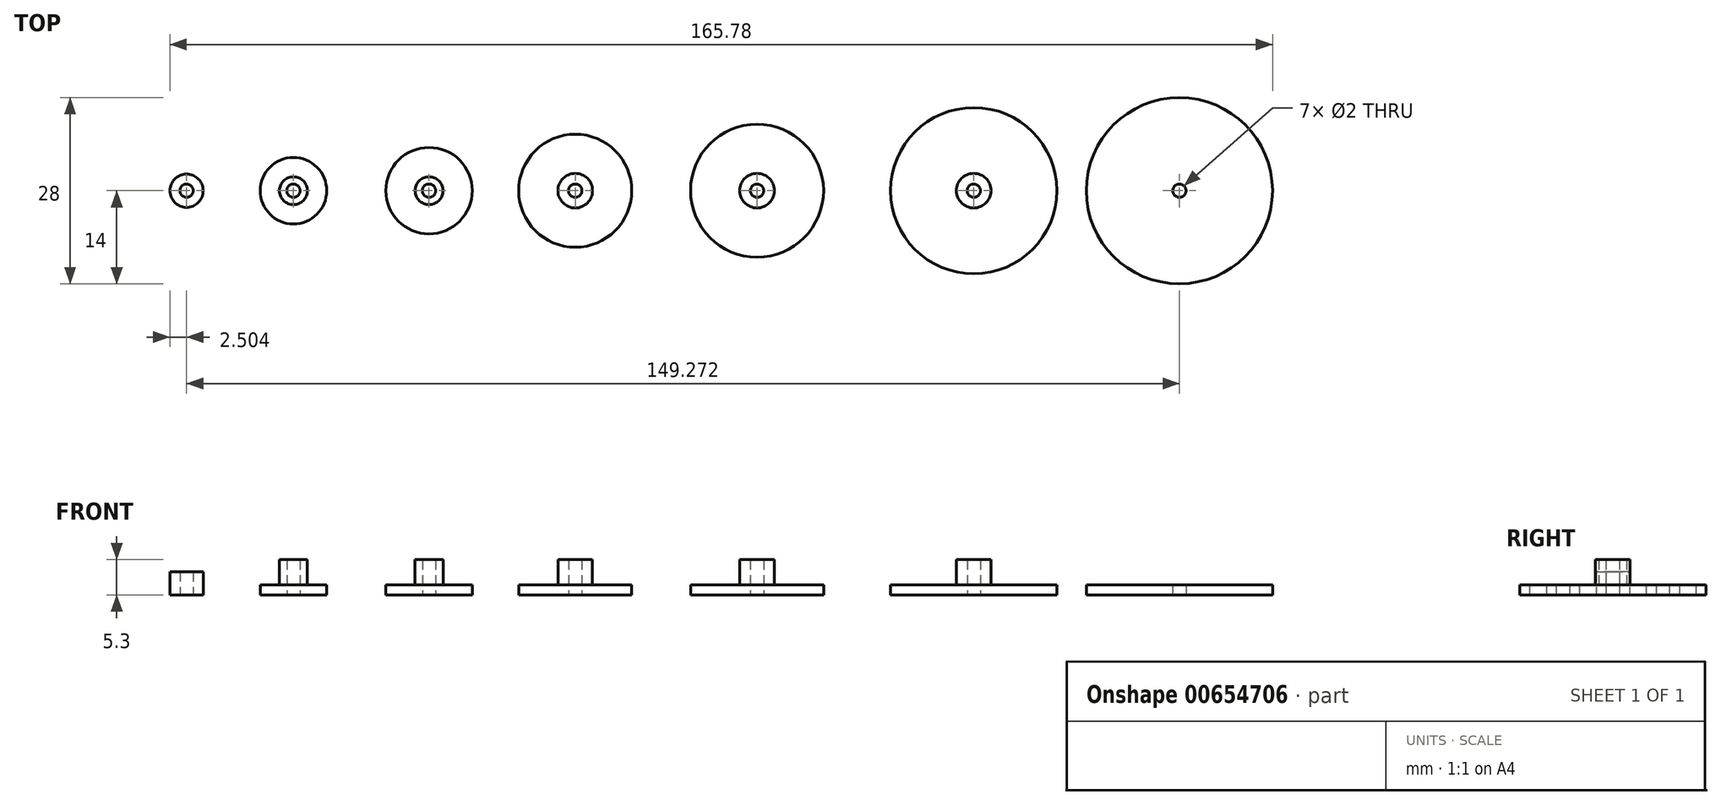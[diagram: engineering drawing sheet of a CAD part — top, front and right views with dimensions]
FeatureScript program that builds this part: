
annotation { "Feature Type Name" : "Feature", "Feature Type Description" : "" }
export const myFeature = defineFeature(function(context is Context, id is Id, definition is map)
    precondition{}
    {
        {
            var Q0;
            Q0=qCreatedBy(makeId("Top.planeOp"),FACE);
            var sketch = newSketch(context, id + "F0", { "sketchPlane" : qUnion([Q0])});
            skCircle(sketch, "E0", {"center": v(0, 0) * mm, "radius": 8.5 * mm});
            skCircle(sketch, "E1", {"center": v(0, 0) * mm, "radius": 1 * mm});
            skSolve(sketch);
        }
        {
            var Q0;
            Q0=makeQuery(id+"F0.imprint","IMPRINT",FACE,{"disambiguationData":[TD([[makeQuery(id+"F0.imprint","IMPRINT",EDGE,{"derivedFrom":sQuery(id+"F0.wireOp",EDGE,"E1")}),-1.0]])]});
            var Q1;
            {var subQ0=sQuery(id+"F0.wireOp",EDGE,"EI4zZE9N-whVI-OPHs-3LS9-Eucb53RtoGpZ");var subQ1=sQuery(id+"F0.wireOp",EDGE,"E0");var subQ2=makeQuery(id+"F0.imprint","INTERSECT",VERTEX,{"derivedFrom":[subQ1,subQ0]});Q1=makeQuery(id+"F0.imprint","IMPRINT",FACE,{"disambiguationData":[TD([[makeQuery(id+"F0.imprint","IMPRINT",EDGE,{"disambiguationData":[TD([[subQ2,1.0]])],"derivedFrom":subQ1}),-1.0]])]});}
            var Q2;
            {var subQ0=sQuery(id+"F0.wireOp",EDGE,"6d7b41f3-6400-49b5-a72e-f197a9a28993.24.0");var subQ1=sQuery(id+"F0.wireOp",EDGE,"E0");var subQ2=makeQuery(id+"F0.imprint","INTERSECT",VERTEX,{"derivedFrom":[subQ1,subQ0]});Q2=makeQuery(id+"F0.imprint","IMPRINT",FACE,{"disambiguationData":[TD([[makeQuery(id+"F0.imprint","IMPRINT",EDGE,{"disambiguationData":[TD([[subQ2,1.0]])],"derivedFrom":subQ1}),-1.0]])]});}
            var Q3;
            {var subQ0=sQuery(id+"F0.wireOp",EDGE,"6d7b41f3-6400-49b5-a72e-f197a9a28993.25.0");var subQ1=sQuery(id+"F0.wireOp",EDGE,"E0");var subQ2=makeQuery(id+"F0.imprint","INTERSECT",VERTEX,{"derivedFrom":[subQ1,subQ0]});Q3=makeQuery(id+"F0.imprint","IMPRINT",FACE,{"disambiguationData":[TD([[makeQuery(id+"F0.imprint","IMPRINT",EDGE,{"disambiguationData":[TD([[subQ2,1.0]])],"derivedFrom":subQ1}),-1.0]])]});}
            var Q4;
            {var subQ0=sQuery(id+"F0.wireOp",EDGE,"6d7b41f3-6400-49b5-a72e-f197a9a28993.26.0");var subQ1=sQuery(id+"F0.wireOp",EDGE,"E0");var subQ2=makeQuery(id+"F0.imprint","INTERSECT",VERTEX,{"derivedFrom":[subQ1,subQ0]});Q4=makeQuery(id+"F0.imprint","IMPRINT",FACE,{"disambiguationData":[TD([[makeQuery(id+"F0.imprint","IMPRINT",EDGE,{"disambiguationData":[TD([[subQ2,1.0]])],"derivedFrom":subQ1}),-1.0]])]});}
            var Q5;
            {var subQ0=sQuery(id+"F0.wireOp",EDGE,"6d7b41f3-6400-49b5-a72e-f197a9a28993.27.0");var subQ1=sQuery(id+"F0.wireOp",EDGE,"E0");var subQ2=makeQuery(id+"F0.imprint","INTERSECT",VERTEX,{"derivedFrom":[subQ1,subQ0]});Q5=makeQuery(id+"F0.imprint","IMPRINT",FACE,{"disambiguationData":[TD([[makeQuery(id+"F0.imprint","IMPRINT",EDGE,{"disambiguationData":[TD([[subQ2,1.0]])],"derivedFrom":subQ1}),-1.0]])]});}
            var Q6;
            {var subQ0=sQuery(id+"F0.wireOp",EDGE,"6d7b41f3-6400-49b5-a72e-f197a9a28993.28.0");var subQ1=sQuery(id+"F0.wireOp",EDGE,"E0");var subQ2=makeQuery(id+"F0.imprint","INTERSECT",VERTEX,{"derivedFrom":[subQ1,subQ0]});Q6=makeQuery(id+"F0.imprint","IMPRINT",FACE,{"disambiguationData":[TD([[makeQuery(id+"F0.imprint","IMPRINT",EDGE,{"disambiguationData":[TD([[subQ2,1.0]])],"derivedFrom":subQ1}),-1.0]])]});}
            var Q7;
            {var subQ0=sQuery(id+"F0.wireOp",EDGE,"6d7b41f3-6400-49b5-a72e-f197a9a28993.29.0");var subQ1=sQuery(id+"F0.wireOp",EDGE,"E0");var subQ2=makeQuery(id+"F0.imprint","INTERSECT",VERTEX,{"derivedFrom":[subQ1,subQ0]});Q7=makeQuery(id+"F0.imprint","IMPRINT",FACE,{"disambiguationData":[TD([[makeQuery(id+"F0.imprint","IMPRINT",EDGE,{"disambiguationData":[TD([[subQ2,1.0]])],"derivedFrom":subQ1}),-1.0]])]});}
            var Q8;
            {var subQ0=sQuery(id+"F0.wireOp",EDGE,"6d7b41f3-6400-49b5-a72e-f197a9a28993.30.0");var subQ1=sQuery(id+"F0.wireOp",EDGE,"E0");var subQ2=makeQuery(id+"F0.imprint","INTERSECT",VERTEX,{"derivedFrom":[subQ1,subQ0]});Q8=makeQuery(id+"F0.imprint","IMPRINT",FACE,{"disambiguationData":[TD([[makeQuery(id+"F0.imprint","IMPRINT",EDGE,{"disambiguationData":[TD([[subQ2,1.0]])],"derivedFrom":subQ1}),-1.0]])]});}
            var Q9;
            {var subQ0=sQuery(id+"F0.wireOp",EDGE,"rxgSa6x3-vu4U-r9f0-bHfC-lMe1TVJ3Zobz");var subQ1=sQuery(id+"F0.wireOp",EDGE,"E0");var subQ2=makeQuery(id+"F0.imprint","INTERSECT",VERTEX,{"derivedFrom":[subQ1,subQ0]});Q9=makeQuery(id+"F0.imprint","IMPRINT",FACE,{"disambiguationData":[TD([[makeQuery(id+"F0.imprint","IMPRINT",EDGE,{"disambiguationData":[TD([[subQ2,-1.0]])],"derivedFrom":subQ1}),-1.0]])]});}
            var Q10;
            {var subQ0=sQuery(id+"F0.wireOp",EDGE,"6d7b41f3-6400-49b5-a72e-f197a9a28993.1.0");var subQ1=sQuery(id+"F0.wireOp",EDGE,"E0");var subQ2=makeQuery(id+"F0.imprint","INTERSECT",VERTEX,{"derivedFrom":[subQ1,subQ0]});Q10=makeQuery(id+"F0.imprint","IMPRINT",FACE,{"disambiguationData":[TD([[makeQuery(id+"F0.imprint","IMPRINT",EDGE,{"disambiguationData":[TD([[subQ2,1.0]])],"derivedFrom":subQ1}),-1.0]])]});}
            var Q11;
            {var subQ0=sQuery(id+"F0.wireOp",EDGE,"6d7b41f3-6400-49b5-a72e-f197a9a28993.2.0");var subQ1=sQuery(id+"F0.wireOp",EDGE,"E0");var subQ2=makeQuery(id+"F0.imprint","INTERSECT",VERTEX,{"derivedFrom":[subQ1,subQ0]});Q11=makeQuery(id+"F0.imprint","IMPRINT",FACE,{"disambiguationData":[TD([[makeQuery(id+"F0.imprint","IMPRINT",EDGE,{"disambiguationData":[TD([[subQ2,1.0]])],"derivedFrom":subQ1}),-1.0]])]});}
            var Q12;
            {var subQ0=sQuery(id+"F0.wireOp",EDGE,"6d7b41f3-6400-49b5-a72e-f197a9a28993.3.0");var subQ1=sQuery(id+"F0.wireOp",EDGE,"E0");var subQ2=makeQuery(id+"F0.imprint","INTERSECT",VERTEX,{"derivedFrom":[subQ1,subQ0]});Q12=makeQuery(id+"F0.imprint","IMPRINT",FACE,{"disambiguationData":[TD([[makeQuery(id+"F0.imprint","IMPRINT",EDGE,{"disambiguationData":[TD([[subQ2,1.0]])],"derivedFrom":subQ1}),-1.0]])]});}
            var Q13;
            {var subQ0=sQuery(id+"F0.wireOp",EDGE,"6d7b41f3-6400-49b5-a72e-f197a9a28993.4.0");var subQ1=sQuery(id+"F0.wireOp",EDGE,"E0");var subQ2=makeQuery(id+"F0.imprint","INTERSECT",VERTEX,{"derivedFrom":[subQ1,subQ0]});Q13=makeQuery(id+"F0.imprint","IMPRINT",FACE,{"disambiguationData":[TD([[makeQuery(id+"F0.imprint","IMPRINT",EDGE,{"disambiguationData":[TD([[subQ2,1.0]])],"derivedFrom":subQ1}),-1.0]])]});}
            var Q14;
            {var subQ0=sQuery(id+"F0.wireOp",EDGE,"6d7b41f3-6400-49b5-a72e-f197a9a28993.5.0");var subQ1=sQuery(id+"F0.wireOp",EDGE,"E0");var subQ2=makeQuery(id+"F0.imprint","INTERSECT",VERTEX,{"derivedFrom":[subQ1,subQ0]});Q14=makeQuery(id+"F0.imprint","IMPRINT",FACE,{"disambiguationData":[TD([[makeQuery(id+"F0.imprint","IMPRINT",EDGE,{"disambiguationData":[TD([[subQ2,1.0]])],"derivedFrom":subQ1}),-1.0]])]});}
            var Q15;
            {var subQ0=sQuery(id+"F0.wireOp",EDGE,"6d7b41f3-6400-49b5-a72e-f197a9a28993.6.0");var subQ1=sQuery(id+"F0.wireOp",EDGE,"E0");var subQ2=makeQuery(id+"F0.imprint","INTERSECT",VERTEX,{"derivedFrom":[subQ1,subQ0]});Q15=makeQuery(id+"F0.imprint","IMPRINT",FACE,{"disambiguationData":[TD([[makeQuery(id+"F0.imprint","IMPRINT",EDGE,{"disambiguationData":[TD([[subQ2,1.0]])],"derivedFrom":subQ1}),-1.0]])]});}
            var Q16;
            {var subQ0=sQuery(id+"F0.wireOp",EDGE,"6d7b41f3-6400-49b5-a72e-f197a9a28993.7.0");var subQ1=sQuery(id+"F0.wireOp",EDGE,"E0");var subQ2=makeQuery(id+"F0.imprint","INTERSECT",VERTEX,{"derivedFrom":[subQ1,subQ0]});Q16=makeQuery(id+"F0.imprint","IMPRINT",FACE,{"disambiguationData":[TD([[makeQuery(id+"F0.imprint","IMPRINT",EDGE,{"disambiguationData":[TD([[subQ2,1.0]])],"derivedFrom":subQ1}),-1.0]])]});}
            var Q17;
            {var subQ0=sQuery(id+"F0.wireOp",EDGE,"6d7b41f3-6400-49b5-a72e-f197a9a28993.8.0");var subQ1=sQuery(id+"F0.wireOp",EDGE,"E0");var subQ2=makeQuery(id+"F0.imprint","INTERSECT",VERTEX,{"derivedFrom":[subQ1,subQ0]});Q17=makeQuery(id+"F0.imprint","IMPRINT",FACE,{"disambiguationData":[TD([[makeQuery(id+"F0.imprint","IMPRINT",EDGE,{"disambiguationData":[TD([[subQ2,1.0]])],"derivedFrom":subQ1}),-1.0]])]});}
            var Q18;
            {var subQ0=sQuery(id+"F0.wireOp",EDGE,"6d7b41f3-6400-49b5-a72e-f197a9a28993.9.0");var subQ1=sQuery(id+"F0.wireOp",EDGE,"E0");var subQ2=makeQuery(id+"F0.imprint","INTERSECT",VERTEX,{"derivedFrom":[subQ1,subQ0]});Q18=makeQuery(id+"F0.imprint","IMPRINT",FACE,{"disambiguationData":[TD([[makeQuery(id+"F0.imprint","IMPRINT",EDGE,{"disambiguationData":[TD([[subQ2,1.0]])],"derivedFrom":subQ1}),-1.0]])]});}
            var Q19;
            {var subQ0=sQuery(id+"F0.wireOp",EDGE,"6d7b41f3-6400-49b5-a72e-f197a9a28993.10.0");var subQ1=sQuery(id+"F0.wireOp",EDGE,"E0");var subQ2=makeQuery(id+"F0.imprint","INTERSECT",VERTEX,{"derivedFrom":[subQ1,subQ0]});Q19=makeQuery(id+"F0.imprint","IMPRINT",FACE,{"disambiguationData":[TD([[makeQuery(id+"F0.imprint","IMPRINT",EDGE,{"disambiguationData":[TD([[subQ2,1.0]])],"derivedFrom":subQ1}),-1.0]])]});}
            var Q20;
            {var subQ0=sQuery(id+"F0.wireOp",EDGE,"6d7b41f3-6400-49b5-a72e-f197a9a28993.11.0");var subQ1=sQuery(id+"F0.wireOp",EDGE,"E0");var subQ2=makeQuery(id+"F0.imprint","INTERSECT",VERTEX,{"derivedFrom":[subQ1,subQ0]});Q20=makeQuery(id+"F0.imprint","IMPRINT",FACE,{"disambiguationData":[TD([[makeQuery(id+"F0.imprint","IMPRINT",EDGE,{"disambiguationData":[TD([[subQ2,1.0]])],"derivedFrom":subQ1}),-1.0]])]});}
            var Q21;
            {var subQ0=sQuery(id+"F0.wireOp",EDGE,"6d7b41f3-6400-49b5-a72e-f197a9a28993.12.0");var subQ1=sQuery(id+"F0.wireOp",EDGE,"E0");var subQ2=makeQuery(id+"F0.imprint","INTERSECT",VERTEX,{"derivedFrom":[subQ1,subQ0]});Q21=makeQuery(id+"F0.imprint","IMPRINT",FACE,{"disambiguationData":[TD([[makeQuery(id+"F0.imprint","IMPRINT",EDGE,{"disambiguationData":[TD([[subQ2,1.0]])],"derivedFrom":subQ1}),-1.0]])]});}
            var Q22;
            {var subQ0=sQuery(id+"F0.wireOp",EDGE,"6d7b41f3-6400-49b5-a72e-f197a9a28993.13.0");var subQ1=sQuery(id+"F0.wireOp",EDGE,"E0");var subQ2=makeQuery(id+"F0.imprint","INTERSECT",VERTEX,{"derivedFrom":[subQ1,subQ0]});Q22=makeQuery(id+"F0.imprint","IMPRINT",FACE,{"disambiguationData":[TD([[makeQuery(id+"F0.imprint","IMPRINT",EDGE,{"disambiguationData":[TD([[subQ2,1.0]])],"derivedFrom":subQ1}),-1.0]])]});}
            var Q23;
            {var subQ0=sQuery(id+"F0.wireOp",EDGE,"6d7b41f3-6400-49b5-a72e-f197a9a28993.14.0");var subQ1=sQuery(id+"F0.wireOp",EDGE,"E0");var subQ2=makeQuery(id+"F0.imprint","INTERSECT",VERTEX,{"derivedFrom":[subQ1,subQ0]});Q23=makeQuery(id+"F0.imprint","IMPRINT",FACE,{"disambiguationData":[TD([[makeQuery(id+"F0.imprint","IMPRINT",EDGE,{"disambiguationData":[TD([[subQ2,1.0]])],"derivedFrom":subQ1}),-1.0]])]});}
            var Q24;
            {var subQ0=sQuery(id+"F0.wireOp",EDGE,"6d7b41f3-6400-49b5-a72e-f197a9a28993.15.0");var subQ1=sQuery(id+"F0.wireOp",EDGE,"E0");var subQ2=makeQuery(id+"F0.imprint","INTERSECT",VERTEX,{"derivedFrom":[subQ1,subQ0]});Q24=makeQuery(id+"F0.imprint","IMPRINT",FACE,{"disambiguationData":[TD([[makeQuery(id+"F0.imprint","IMPRINT",EDGE,{"disambiguationData":[TD([[subQ2,1.0]])],"derivedFrom":subQ1}),-1.0]])]});}
            var Q25;
            {var subQ0=sQuery(id+"F0.wireOp",EDGE,"6d7b41f3-6400-49b5-a72e-f197a9a28993.16.0");var subQ1=sQuery(id+"F0.wireOp",EDGE,"E0");var subQ2=makeQuery(id+"F0.imprint","INTERSECT",VERTEX,{"derivedFrom":[subQ1,subQ0]});Q25=makeQuery(id+"F0.imprint","IMPRINT",FACE,{"disambiguationData":[TD([[makeQuery(id+"F0.imprint","IMPRINT",EDGE,{"disambiguationData":[TD([[subQ2,1.0]])],"derivedFrom":subQ1}),-1.0]])]});}
            var Q26;
            {var subQ0=sQuery(id+"F0.wireOp",EDGE,"6d7b41f3-6400-49b5-a72e-f197a9a28993.17.0");var subQ1=sQuery(id+"F0.wireOp",EDGE,"E0");var subQ2=makeQuery(id+"F0.imprint","INTERSECT",VERTEX,{"derivedFrom":[subQ1,subQ0]});Q26=makeQuery(id+"F0.imprint","IMPRINT",FACE,{"disambiguationData":[TD([[makeQuery(id+"F0.imprint","IMPRINT",EDGE,{"disambiguationData":[TD([[subQ2,1.0]])],"derivedFrom":subQ1}),-1.0]])]});}
            var Q27;
            {var subQ0=sQuery(id+"F0.wireOp",EDGE,"6d7b41f3-6400-49b5-a72e-f197a9a28993.18.0");var subQ1=sQuery(id+"F0.wireOp",EDGE,"E0");var subQ2=makeQuery(id+"F0.imprint","INTERSECT",VERTEX,{"derivedFrom":[subQ1,subQ0]});Q27=makeQuery(id+"F0.imprint","IMPRINT",FACE,{"disambiguationData":[TD([[makeQuery(id+"F0.imprint","IMPRINT",EDGE,{"disambiguationData":[TD([[subQ2,1.0]])],"derivedFrom":subQ1}),-1.0]])]});}
            var Q28;
            {var subQ0=sQuery(id+"F0.wireOp",EDGE,"6d7b41f3-6400-49b5-a72e-f197a9a28993.19.0");var subQ1=sQuery(id+"F0.wireOp",EDGE,"E0");var subQ2=makeQuery(id+"F0.imprint","INTERSECT",VERTEX,{"derivedFrom":[subQ1,subQ0]});Q28=makeQuery(id+"F0.imprint","IMPRINT",FACE,{"disambiguationData":[TD([[makeQuery(id+"F0.imprint","IMPRINT",EDGE,{"disambiguationData":[TD([[subQ2,1.0]])],"derivedFrom":subQ1}),-1.0]])]});}
            var Q29;
            {var subQ0=sQuery(id+"F0.wireOp",EDGE,"6d7b41f3-6400-49b5-a72e-f197a9a28993.20.0");var subQ1=sQuery(id+"F0.wireOp",EDGE,"E0");var subQ2=makeQuery(id+"F0.imprint","INTERSECT",VERTEX,{"derivedFrom":[subQ1,subQ0]});Q29=makeQuery(id+"F0.imprint","IMPRINT",FACE,{"disambiguationData":[TD([[makeQuery(id+"F0.imprint","IMPRINT",EDGE,{"disambiguationData":[TD([[subQ2,1.0]])],"derivedFrom":subQ1}),-1.0]])]});}
            var Q30;
            {var subQ0=sQuery(id+"F0.wireOp",EDGE,"6d7b41f3-6400-49b5-a72e-f197a9a28993.21.0");var subQ1=sQuery(id+"F0.wireOp",EDGE,"E0");var subQ2=makeQuery(id+"F0.imprint","INTERSECT",VERTEX,{"derivedFrom":[subQ1,subQ0]});Q30=makeQuery(id+"F0.imprint","IMPRINT",FACE,{"disambiguationData":[TD([[makeQuery(id+"F0.imprint","IMPRINT",EDGE,{"disambiguationData":[TD([[subQ2,1.0]])],"derivedFrom":subQ1}),-1.0]])]});}
            var Q31;
            {var subQ0=sQuery(id+"F0.wireOp",EDGE,"6d7b41f3-6400-49b5-a72e-f197a9a28993.22.0");var subQ1=sQuery(id+"F0.wireOp",EDGE,"E0");var subQ2=makeQuery(id+"F0.imprint","INTERSECT",VERTEX,{"derivedFrom":[subQ1,subQ0]});Q31=makeQuery(id+"F0.imprint","IMPRINT",FACE,{"disambiguationData":[TD([[makeQuery(id+"F0.imprint","IMPRINT",EDGE,{"disambiguationData":[TD([[subQ2,1.0]])],"derivedFrom":subQ1}),-1.0]])]});}
            var Q32;
            {var subQ0=sQuery(id+"F0.wireOp",EDGE,"6d7b41f3-6400-49b5-a72e-f197a9a28993.23.0");var subQ1=sQuery(id+"F0.wireOp",EDGE,"E0");var subQ2=makeQuery(id+"F0.imprint","INTERSECT",VERTEX,{"derivedFrom":[subQ1,subQ0]});Q32=makeQuery(id+"F0.imprint","IMPRINT",FACE,{"disambiguationData":[TD([[makeQuery(id+"F0.imprint","IMPRINT",EDGE,{"disambiguationData":[TD([[subQ2,1.0]])],"derivedFrom":subQ1}),-1.0]])]});}
            var Q33;
            {var subQ3=sQuery(id+"F0.wireOp",EDGE,"rxgSa6x3-vu4U-r9f0-bHfC-lMe1TVJ3Zobz");var subQ6=sQuery(id+"F0.wireOp",EDGE,"E0");var subQ9=makeQuery(id+"F0.imprint","INTERSECT",VERTEX,{"derivedFrom":[subQ6,subQ3]});Q33=makeQuery(id+"F0.imprint","IMPRINT",FACE,{"disambiguationData":[TD([[makeQuery(id+"F0.imprint","IMPRINT",EDGE,{"disambiguationData":[TD([[subQ9,1.0]])],"derivedFrom":subQ6}),-1.0]])]});}
            var Q34;
            {var subQ3=sQuery(id+"F0.wireOp",EDGE,"EI4zZE9N-whVI-OPHs-3LS9-Eucb53RtoGpZ");var subQ7=sQuery(id+"F0.wireOp",EDGE,"E0");var subQ8=makeQuery(id+"F0.imprint","INTERSECT",VERTEX,{"derivedFrom":[subQ7,subQ3]});Q34=makeQuery(id+"F0.imprint","IMPRINT",FACE,{"disambiguationData":[TD([[makeQuery(id+"F0.imprint","IMPRINT",EDGE,{"disambiguationData":[TD([[subQ8,-1.0]])],"derivedFrom":subQ7}),-1.0]])]});}
            var Q35;
            {var subQ3=sQuery(id+"F0.wireOp",EDGE,"6d7b41f3-6400-49b5-a72e-f197a9a28993.6.0");var subQ5=sQuery(id+"F0.wireOp",EDGE,"E0");var subQ6=makeQuery(id+"F0.imprint","INTERSECT",VERTEX,{"derivedFrom":[subQ5,subQ3]});Q35=makeQuery(id+"F0.imprint","IMPRINT",FACE,{"disambiguationData":[TD([[makeQuery(id+"F0.imprint","IMPRINT",EDGE,{"disambiguationData":[TD([[subQ6,-1.0]])],"derivedFrom":subQ5}),-1.0]])]});}
            var Q36;
            {var subQ3=sQuery(id+"F0.wireOp",EDGE,"6d7b41f3-6400-49b5-a72e-f197a9a28993.24.0");var subQ7=sQuery(id+"F0.wireOp",EDGE,"E0");var subQ8=makeQuery(id+"F0.imprint","INTERSECT",VERTEX,{"derivedFrom":[subQ7,subQ3]});Q36=makeQuery(id+"F0.imprint","IMPRINT",FACE,{"disambiguationData":[TD([[makeQuery(id+"F0.imprint","IMPRINT",EDGE,{"disambiguationData":[TD([[subQ8,-1.0]])],"derivedFrom":subQ7}),-1.0]])]});}
            var Q37;
            {var subQ3=sQuery(id+"F0.wireOp",EDGE,"6d7b41f3-6400-49b5-a72e-f197a9a28993.14.0");var subQ7=sQuery(id+"F0.wireOp",EDGE,"E0");var subQ8=makeQuery(id+"F0.imprint","INTERSECT",VERTEX,{"derivedFrom":[subQ7,subQ3]});Q37=makeQuery(id+"F0.imprint","IMPRINT",FACE,{"disambiguationData":[TD([[makeQuery(id+"F0.imprint","IMPRINT",EDGE,{"disambiguationData":[TD([[subQ8,-1.0]])],"derivedFrom":subQ7}),-1.0]])]});}
            var Q38;
            {var subQ5=sQuery(id+"F0.wireOp",EDGE,"6d7b41f3-6400-49b5-a72e-f197a9a28993.26.0");var subQ6=sQuery(id+"F0.wireOp",EDGE,"E0");var subQ7=makeQuery(id+"F0.imprint","INTERSECT",VERTEX,{"derivedFrom":[subQ6,subQ5]});Q38=makeQuery(id+"F0.imprint","IMPRINT",FACE,{"disambiguationData":[TD([[makeQuery(id+"F0.imprint","IMPRINT",EDGE,{"disambiguationData":[TD([[subQ7,-1.0]])],"derivedFrom":subQ6}),-1.0]])]});}
            var Q39;
            {var subQ3=sQuery(id+"F0.wireOp",EDGE,"6d7b41f3-6400-49b5-a72e-f197a9a28993.9.0");var subQ7=sQuery(id+"F0.wireOp",EDGE,"E0");var subQ8=makeQuery(id+"F0.imprint","INTERSECT",VERTEX,{"derivedFrom":[subQ7,subQ3]});Q39=makeQuery(id+"F0.imprint","IMPRINT",FACE,{"disambiguationData":[TD([[makeQuery(id+"F0.imprint","IMPRINT",EDGE,{"disambiguationData":[TD([[subQ8,-1.0]])],"derivedFrom":subQ7}),-1.0]])]});}
            var Q40;
            {var subQ3=sQuery(id+"F0.wireOp",EDGE,"6d7b41f3-6400-49b5-a72e-f197a9a28993.7.0");var subQ7=sQuery(id+"F0.wireOp",EDGE,"E0");var subQ8=makeQuery(id+"F0.imprint","INTERSECT",VERTEX,{"derivedFrom":[subQ7,subQ3]});Q40=makeQuery(id+"F0.imprint","IMPRINT",FACE,{"disambiguationData":[TD([[makeQuery(id+"F0.imprint","IMPRINT",EDGE,{"disambiguationData":[TD([[subQ8,-1.0]])],"derivedFrom":subQ7}),-1.0]])]});}
            var Q41;
            {var subQ3=sQuery(id+"F0.wireOp",EDGE,"6d7b41f3-6400-49b5-a72e-f197a9a28993.22.0");var subQ7=sQuery(id+"F0.wireOp",EDGE,"E0");var subQ8=makeQuery(id+"F0.imprint","INTERSECT",VERTEX,{"derivedFrom":[subQ7,subQ3]});Q41=makeQuery(id+"F0.imprint","IMPRINT",FACE,{"disambiguationData":[TD([[makeQuery(id+"F0.imprint","IMPRINT",EDGE,{"disambiguationData":[TD([[subQ8,-1.0]])],"derivedFrom":subQ7}),-1.0]])]});}
            var Q42;
            {var subQ5=sQuery(id+"F0.wireOp",EDGE,"6d7b41f3-6400-49b5-a72e-f197a9a28993.23.0");var subQ6=sQuery(id+"F0.wireOp",EDGE,"E0");var subQ7=makeQuery(id+"F0.imprint","INTERSECT",VERTEX,{"derivedFrom":[subQ6,subQ5]});Q42=makeQuery(id+"F0.imprint","IMPRINT",FACE,{"disambiguationData":[TD([[makeQuery(id+"F0.imprint","IMPRINT",EDGE,{"disambiguationData":[TD([[subQ7,-1.0]])],"derivedFrom":subQ6}),-1.0]])]});}
            var Q43;
            {var subQ3=sQuery(id+"F0.wireOp",EDGE,"6d7b41f3-6400-49b5-a72e-f197a9a28993.4.0");var subQ7=sQuery(id+"F0.wireOp",EDGE,"E0");var subQ8=makeQuery(id+"F0.imprint","INTERSECT",VERTEX,{"derivedFrom":[subQ7,subQ3]});Q43=makeQuery(id+"F0.imprint","IMPRINT",FACE,{"disambiguationData":[TD([[makeQuery(id+"F0.imprint","IMPRINT",EDGE,{"disambiguationData":[TD([[subQ8,-1.0]])],"derivedFrom":subQ7}),-1.0]])]});}
            var Q44;
            {var subQ0=sQuery(id+"F0.wireOp",EDGE,"6d7b41f3-6400-49b5-a72e-f197a9a28993.1.1");var subQ1=sQuery(id+"F0.wireOp",EDGE,"E0");var subQ2=makeQuery(id+"F0.imprint","INTERSECT",VERTEX,{"derivedFrom":[subQ1,subQ0]});Q44=makeQuery(id+"F0.imprint","IMPRINT",FACE,{"disambiguationData":[TD([[makeQuery(id+"F0.imprint","IMPRINT",EDGE,{"disambiguationData":[TD([[subQ2,1.0]])],"derivedFrom":subQ1}),-1.0]])]});}
            var Q45;
            {var subQ3=sQuery(id+"F0.wireOp",EDGE,"6d7b41f3-6400-49b5-a72e-f197a9a28993.10.0");var subQ7=sQuery(id+"F0.wireOp",EDGE,"E0");var subQ8=makeQuery(id+"F0.imprint","INTERSECT",VERTEX,{"derivedFrom":[subQ7,subQ3]});Q45=makeQuery(id+"F0.imprint","IMPRINT",FACE,{"disambiguationData":[TD([[makeQuery(id+"F0.imprint","IMPRINT",EDGE,{"disambiguationData":[TD([[subQ8,-1.0]])],"derivedFrom":subQ7}),-1.0]])]});}
            var Q46;
            {var subQ3=sQuery(id+"F0.wireOp",EDGE,"6d7b41f3-6400-49b5-a72e-f197a9a28993.21.0");var subQ7=sQuery(id+"F0.wireOp",EDGE,"E0");var subQ8=makeQuery(id+"F0.imprint","INTERSECT",VERTEX,{"derivedFrom":[subQ7,subQ3]});Q46=makeQuery(id+"F0.imprint","IMPRINT",FACE,{"disambiguationData":[TD([[makeQuery(id+"F0.imprint","IMPRINT",EDGE,{"disambiguationData":[TD([[subQ8,-1.0]])],"derivedFrom":subQ7}),-1.0]])]});}
            var Q47;
            {var subQ3=sQuery(id+"F0.wireOp",EDGE,"6d7b41f3-6400-49b5-a72e-f197a9a28993.2.0");var subQ7=sQuery(id+"F0.wireOp",EDGE,"E0");var subQ8=makeQuery(id+"F0.imprint","INTERSECT",VERTEX,{"derivedFrom":[subQ7,subQ3]});Q47=makeQuery(id+"F0.imprint","IMPRINT",FACE,{"disambiguationData":[TD([[makeQuery(id+"F0.imprint","IMPRINT",EDGE,{"disambiguationData":[TD([[subQ8,-1.0]])],"derivedFrom":subQ7}),-1.0]])]});}
            var Q48;
            {var subQ3=sQuery(id+"F0.wireOp",EDGE,"6d7b41f3-6400-49b5-a72e-f197a9a28993.27.0");var subQ7=sQuery(id+"F0.wireOp",EDGE,"E0");var subQ8=makeQuery(id+"F0.imprint","INTERSECT",VERTEX,{"derivedFrom":[subQ7,subQ3]});Q48=makeQuery(id+"F0.imprint","IMPRINT",FACE,{"disambiguationData":[TD([[makeQuery(id+"F0.imprint","IMPRINT",EDGE,{"disambiguationData":[TD([[subQ8,-1.0]])],"derivedFrom":subQ7}),-1.0]])]});}
            var Q49;
            {var subQ3=sQuery(id+"F0.wireOp",EDGE,"6d7b41f3-6400-49b5-a72e-f197a9a28993.15.0");var subQ7=sQuery(id+"F0.wireOp",EDGE,"E0");var subQ8=makeQuery(id+"F0.imprint","INTERSECT",VERTEX,{"derivedFrom":[subQ7,subQ3]});Q49=makeQuery(id+"F0.imprint","IMPRINT",FACE,{"disambiguationData":[TD([[makeQuery(id+"F0.imprint","IMPRINT",EDGE,{"disambiguationData":[TD([[subQ8,-1.0]])],"derivedFrom":subQ7}),-1.0]])]});}
            var Q50;
            {var subQ3=sQuery(id+"F0.wireOp",EDGE,"6d7b41f3-6400-49b5-a72e-f197a9a28993.16.0");var subQ7=sQuery(id+"F0.wireOp",EDGE,"E0");var subQ8=makeQuery(id+"F0.imprint","INTERSECT",VERTEX,{"derivedFrom":[subQ7,subQ3]});Q50=makeQuery(id+"F0.imprint","IMPRINT",FACE,{"disambiguationData":[TD([[makeQuery(id+"F0.imprint","IMPRINT",EDGE,{"disambiguationData":[TD([[subQ8,-1.0]])],"derivedFrom":subQ7}),-1.0]])]});}
            var Q51;
            {var subQ5=sQuery(id+"F0.wireOp",EDGE,"6d7b41f3-6400-49b5-a72e-f197a9a28993.8.0");var subQ6=sQuery(id+"F0.wireOp",EDGE,"E0");var subQ7=makeQuery(id+"F0.imprint","INTERSECT",VERTEX,{"derivedFrom":[subQ6,subQ5]});Q51=makeQuery(id+"F0.imprint","IMPRINT",FACE,{"disambiguationData":[TD([[makeQuery(id+"F0.imprint","IMPRINT",EDGE,{"disambiguationData":[TD([[subQ7,-1.0]])],"derivedFrom":subQ6}),-1.0]])]});}
            var Q52;
            {var subQ3=sQuery(id+"F0.wireOp",EDGE,"6d7b41f3-6400-49b5-a72e-f197a9a28993.25.0");var subQ7=sQuery(id+"F0.wireOp",EDGE,"E0");var subQ8=makeQuery(id+"F0.imprint","INTERSECT",VERTEX,{"derivedFrom":[subQ7,subQ3]});Q52=makeQuery(id+"F0.imprint","IMPRINT",FACE,{"disambiguationData":[TD([[makeQuery(id+"F0.imprint","IMPRINT",EDGE,{"disambiguationData":[TD([[subQ8,-1.0]])],"derivedFrom":subQ7}),-1.0]])]});}
            var Q53;
            {var subQ5=sQuery(id+"F0.wireOp",EDGE,"6d7b41f3-6400-49b5-a72e-f197a9a28993.18.0");var subQ6=sQuery(id+"F0.wireOp",EDGE,"E0");var subQ7=makeQuery(id+"F0.imprint","INTERSECT",VERTEX,{"derivedFrom":[subQ6,subQ5]});Q53=makeQuery(id+"F0.imprint","IMPRINT",FACE,{"disambiguationData":[TD([[makeQuery(id+"F0.imprint","IMPRINT",EDGE,{"disambiguationData":[TD([[subQ7,-1.0]])],"derivedFrom":subQ6}),-1.0]])]});}
            var Q54;
            {var subQ3=sQuery(id+"F0.wireOp",EDGE,"6d7b41f3-6400-49b5-a72e-f197a9a28993.5.0");var subQ7=sQuery(id+"F0.wireOp",EDGE,"E0");var subQ8=makeQuery(id+"F0.imprint","INTERSECT",VERTEX,{"derivedFrom":[subQ7,subQ3]});Q54=makeQuery(id+"F0.imprint","IMPRINT",FACE,{"disambiguationData":[TD([[makeQuery(id+"F0.imprint","IMPRINT",EDGE,{"disambiguationData":[TD([[subQ8,-1.0]])],"derivedFrom":subQ7}),-1.0]])]});}
            var Q55;
            {var subQ3=sQuery(id+"F0.wireOp",EDGE,"6d7b41f3-6400-49b5-a72e-f197a9a28993.28.0");var subQ7=sQuery(id+"F0.wireOp",EDGE,"E0");var subQ8=makeQuery(id+"F0.imprint","INTERSECT",VERTEX,{"derivedFrom":[subQ7,subQ3]});Q55=makeQuery(id+"F0.imprint","IMPRINT",FACE,{"disambiguationData":[TD([[makeQuery(id+"F0.imprint","IMPRINT",EDGE,{"disambiguationData":[TD([[subQ8,-1.0]])],"derivedFrom":subQ7}),-1.0]])]});}
            var Q56;
            {var subQ3=sQuery(id+"F0.wireOp",EDGE,"6d7b41f3-6400-49b5-a72e-f197a9a28993.11.0");var subQ7=sQuery(id+"F0.wireOp",EDGE,"E0");var subQ8=makeQuery(id+"F0.imprint","INTERSECT",VERTEX,{"derivedFrom":[subQ7,subQ3]});Q56=makeQuery(id+"F0.imprint","IMPRINT",FACE,{"disambiguationData":[TD([[makeQuery(id+"F0.imprint","IMPRINT",EDGE,{"disambiguationData":[TD([[subQ8,-1.0]])],"derivedFrom":subQ7}),-1.0]])]});}
            var Q57;
            {var subQ3=sQuery(id+"F0.wireOp",EDGE,"6d7b41f3-6400-49b5-a72e-f197a9a28993.12.0");var subQ7=sQuery(id+"F0.wireOp",EDGE,"E0");var subQ8=makeQuery(id+"F0.imprint","INTERSECT",VERTEX,{"derivedFrom":[subQ7,subQ3]});Q57=makeQuery(id+"F0.imprint","IMPRINT",FACE,{"disambiguationData":[TD([[makeQuery(id+"F0.imprint","IMPRINT",EDGE,{"disambiguationData":[TD([[subQ8,-1.0]])],"derivedFrom":subQ7}),-1.0]])]});}
            var Q58;
            {var subQ3=sQuery(id+"F0.wireOp",EDGE,"6d7b41f3-6400-49b5-a72e-f197a9a28993.19.0");var subQ7=sQuery(id+"F0.wireOp",EDGE,"E0");var subQ8=makeQuery(id+"F0.imprint","INTERSECT",VERTEX,{"derivedFrom":[subQ7,subQ3]});Q58=makeQuery(id+"F0.imprint","IMPRINT",FACE,{"disambiguationData":[TD([[makeQuery(id+"F0.imprint","IMPRINT",EDGE,{"disambiguationData":[TD([[subQ8,-1.0]])],"derivedFrom":subQ7}),-1.0]])]});}
            var Q59;
            {var subQ5=sQuery(id+"F0.wireOp",EDGE,"6d7b41f3-6400-49b5-a72e-f197a9a28993.13.0");var subQ6=sQuery(id+"F0.wireOp",EDGE,"E0");var subQ7=makeQuery(id+"F0.imprint","INTERSECT",VERTEX,{"derivedFrom":[subQ6,subQ5]});Q59=makeQuery(id+"F0.imprint","IMPRINT",FACE,{"disambiguationData":[TD([[makeQuery(id+"F0.imprint","IMPRINT",EDGE,{"disambiguationData":[TD([[subQ7,-1.0]])],"derivedFrom":subQ6}),-1.0]])]});}
            var Q60;
            {var subQ3=sQuery(id+"F0.wireOp",EDGE,"6d7b41f3-6400-49b5-a72e-f197a9a28993.20.0");var subQ7=sQuery(id+"F0.wireOp",EDGE,"E0");var subQ8=makeQuery(id+"F0.imprint","INTERSECT",VERTEX,{"derivedFrom":[subQ7,subQ3]});Q60=makeQuery(id+"F0.imprint","IMPRINT",FACE,{"disambiguationData":[TD([[makeQuery(id+"F0.imprint","IMPRINT",EDGE,{"disambiguationData":[TD([[subQ8,-1.0]])],"derivedFrom":subQ7}),-1.0]])]});}
            var Q61;
            {var subQ3=sQuery(id+"F0.wireOp",EDGE,"6d7b41f3-6400-49b5-a72e-f197a9a28993.1.0");var subQ7=sQuery(id+"F0.wireOp",EDGE,"E0");var subQ8=makeQuery(id+"F0.imprint","INTERSECT",VERTEX,{"derivedFrom":[subQ7,subQ3]});Q61=makeQuery(id+"F0.imprint","IMPRINT",FACE,{"disambiguationData":[TD([[makeQuery(id+"F0.imprint","IMPRINT",EDGE,{"disambiguationData":[TD([[subQ8,-1.0]])],"derivedFrom":subQ7}),-1.0]])]});}
            var Q62;
            {var subQ5=sQuery(id+"F0.wireOp",EDGE,"6d7b41f3-6400-49b5-a72e-f197a9a28993.3.0");var subQ6=sQuery(id+"F0.wireOp",EDGE,"E0");var subQ7=makeQuery(id+"F0.imprint","INTERSECT",VERTEX,{"derivedFrom":[subQ6,subQ5]});Q62=makeQuery(id+"F0.imprint","IMPRINT",FACE,{"disambiguationData":[TD([[makeQuery(id+"F0.imprint","IMPRINT",EDGE,{"disambiguationData":[TD([[subQ7,-1.0]])],"derivedFrom":subQ6}),-1.0]])]});}
            var Q63;
            {var subQ3=sQuery(id+"F0.wireOp",EDGE,"6d7b41f3-6400-49b5-a72e-f197a9a28993.17.0");var subQ5=sQuery(id+"F0.wireOp",EDGE,"E0");var subQ6=makeQuery(id+"F0.imprint","INTERSECT",VERTEX,{"derivedFrom":[subQ5,subQ3]});Q63=makeQuery(id+"F0.imprint","IMPRINT",FACE,{"disambiguationData":[TD([[makeQuery(id+"F0.imprint","IMPRINT",EDGE,{"disambiguationData":[TD([[subQ6,-1.0]])],"derivedFrom":subQ5}),-1.0]])]});}
            var Q64;
            {var subQ3=sQuery(id+"F0.wireOp",EDGE,"6d7b41f3-6400-49b5-a72e-f197a9a28993.29.0");var subQ5=sQuery(id+"F0.wireOp",EDGE,"E0");var subQ6=makeQuery(id+"F0.imprint","INTERSECT",VERTEX,{"derivedFrom":[subQ5,subQ3]});Q64=makeQuery(id+"F0.imprint","IMPRINT",FACE,{"disambiguationData":[TD([[makeQuery(id+"F0.imprint","IMPRINT",EDGE,{"disambiguationData":[TD([[subQ6,-1.0]])],"derivedFrom":subQ5}),-1.0]])]});}
            extrude(context, id + "F1", {"entities" : qUnion([Q0, Q1, Q2, Q3, Q4, Q5, Q6, Q7, Q8, Q9, Q10, Q11, Q12, Q13, Q14, Q15, Q16, Q17, Q18, Q19, Q20, Q21, Q22, Q23, Q24, Q25, Q26, Q27, Q28, Q29, Q30, Q31, Q32, Q33, Q34, Q35, Q36, Q37, Q38, Q39, Q40, Q41, Q42, Q43, Q44, Q45, Q46, Q47, Q48, Q49, Q50, Q51, Q52, Q53, Q54, Q55, Q56, Q57, Q58, Q59, Q60, Q61, Q62, Q63, Q64]), "depth" : 1.5 * mm});
        }
        {
            var Q0;
            Q0=makeQuery(id+"F1.opExtrude","CAP_FACE",FACE,{"disambiguationData":[OSD([sQuery(id+"F0.wireOp",EDGE,"E0"),sQuery(id+"F0.wireOp",EDGE,"E1"),sQuery(id+"F0.wireOp",EDGE,"EI4zZE9N-whVI-OPHs-3LS9-Eucb53RtoGpZ"),sQuery(id+"F0.wireOp",EDGE,"rxgSa6x3-vu4U-r9f0-bHfC-lMe1TVJ3Zobz"),sQuery(id+"F0.wireOp",EDGE,"2ae64cd4-93b4-47b9-bf13-a57fa4e7248b.1.0"),sQuery(id+"F0.wireOp",EDGE,"2ae64cd4-93b4-47b9-bf13-a57fa4e7248b.1.1"),sQuery(id+"F0.wireOp",EDGE,"2ae64cd4-93b4-47b9-bf13-a57fa4e7248b.2.0"),sQuery(id+"F0.wireOp",EDGE,"2ae64cd4-93b4-47b9-bf13-a57fa4e7248b.2.1"),sQuery(id+"F0.wireOp",EDGE,"2ae64cd4-93b4-47b9-bf13-a57fa4e7248b.3.0"),sQuery(id+"F0.wireOp",EDGE,"2ae64cd4-93b4-47b9-bf13-a57fa4e7248b.3.1"),sQuery(id+"F0.wireOp",EDGE,"2ae64cd4-93b4-47b9-bf13-a57fa4e7248b.4.0"),sQuery(id+"F0.wireOp",EDGE,"2ae64cd4-93b4-47b9-bf13-a57fa4e7248b.4.1"),sQuery(id+"F0.wireOp",EDGE,"2ae64cd4-93b4-47b9-bf13-a57fa4e7248b.5.0"),sQuery(id+"F0.wireOp",EDGE,"2ae64cd4-93b4-47b9-bf13-a57fa4e7248b.5.1"),sQuery(id+"F0.wireOp",EDGE,"2ae64cd4-93b4-47b9-bf13-a57fa4e7248b.6.0"),sQuery(id+"F0.wireOp",EDGE,"2ae64cd4-93b4-47b9-bf13-a57fa4e7248b.6.1"),sQuery(id+"F0.wireOp",EDGE,"2ae64cd4-93b4-47b9-bf13-a57fa4e7248b.7.0"),sQuery(id+"F0.wireOp",EDGE,"2ae64cd4-93b4-47b9-bf13-a57fa4e7248b.7.1"),sQuery(id+"F0.wireOp",EDGE,"2ae64cd4-93b4-47b9-bf13-a57fa4e7248b.8.0"),sQuery(id+"F0.wireOp",EDGE,"2ae64cd4-93b4-47b9-bf13-a57fa4e7248b.8.1"),sQuery(id+"F0.wireOp",EDGE,"2ae64cd4-93b4-47b9-bf13-a57fa4e7248b.9.0"),sQuery(id+"F0.wireOp",EDGE,"2ae64cd4-93b4-47b9-bf13-a57fa4e7248b.9.1"),sQuery(id+"F0.wireOp",EDGE,"2ae64cd4-93b4-47b9-bf13-a57fa4e7248b.10.0"),sQuery(id+"F0.wireOp",EDGE,"2ae64cd4-93b4-47b9-bf13-a57fa4e7248b.10.1"),sQuery(id+"F0.wireOp",EDGE,"2ae64cd4-93b4-47b9-bf13-a57fa4e7248b.11.0"),sQuery(id+"F0.wireOp",EDGE,"2ae64cd4-93b4-47b9-bf13-a57fa4e7248b.11.1"),sQuery(id+"F0.wireOp",EDGE,"2ae64cd4-93b4-47b9-bf13-a57fa4e7248b.12.0"),sQuery(id+"F0.wireOp",EDGE,"2ae64cd4-93b4-47b9-bf13-a57fa4e7248b.12.1"),sQuery(id+"F0.wireOp",EDGE,"2ae64cd4-93b4-47b9-bf13-a57fa4e7248b.13.0"),sQuery(id+"F0.wireOp",EDGE,"2ae64cd4-93b4-47b9-bf13-a57fa4e7248b.13.1"),sQuery(id+"F0.wireOp",EDGE,"2ae64cd4-93b4-47b9-bf13-a57fa4e7248b.14.0"),sQuery(id+"F0.wireOp",EDGE,"2ae64cd4-93b4-47b9-bf13-a57fa4e7248b.14.1"),sQuery(id+"F0.wireOp",EDGE,"2ae64cd4-93b4-47b9-bf13-a57fa4e7248b.15.0"),sQuery(id+"F0.wireOp",EDGE,"2ae64cd4-93b4-47b9-bf13-a57fa4e7248b.15.1"),sQuery(id+"F0.wireOp",EDGE,"2ae64cd4-93b4-47b9-bf13-a57fa4e7248b.16.0"),sQuery(id+"F0.wireOp",EDGE,"2ae64cd4-93b4-47b9-bf13-a57fa4e7248b.16.1"),sQuery(id+"F0.wireOp",EDGE,"2ae64cd4-93b4-47b9-bf13-a57fa4e7248b.17.0"),sQuery(id+"F0.wireOp",EDGE,"2ae64cd4-93b4-47b9-bf13-a57fa4e7248b.17.1"),sQuery(id+"F0.wireOp",EDGE,"2ae64cd4-93b4-47b9-bf13-a57fa4e7248b.18.0"),sQuery(id+"F0.wireOp",EDGE,"2ae64cd4-93b4-47b9-bf13-a57fa4e7248b.18.1"),sQuery(id+"F0.wireOp",EDGE,"2ae64cd4-93b4-47b9-bf13-a57fa4e7248b.19.0"),sQuery(id+"F0.wireOp",EDGE,"2ae64cd4-93b4-47b9-bf13-a57fa4e7248b.19.1"),sQuery(id+"F0.wireOp",EDGE,"2ae64cd4-93b4-47b9-bf13-a57fa4e7248b.20.0"),sQuery(id+"F0.wireOp",EDGE,"2ae64cd4-93b4-47b9-bf13-a57fa4e7248b.20.1"),sQuery(id+"F0.wireOp",EDGE,"2ae64cd4-93b4-47b9-bf13-a57fa4e7248b.21.0"),sQuery(id+"F0.wireOp",EDGE,"2ae64cd4-93b4-47b9-bf13-a57fa4e7248b.21.1"),sQuery(id+"F0.wireOp",EDGE,"2ae64cd4-93b4-47b9-bf13-a57fa4e7248b.22.0"),sQuery(id+"F0.wireOp",EDGE,"2ae64cd4-93b4-47b9-bf13-a57fa4e7248b.22.1"),sQuery(id+"F0.wireOp",EDGE,"2ae64cd4-93b4-47b9-bf13-a57fa4e7248b.23.0"),sQuery(id+"F0.wireOp",EDGE,"2ae64cd4-93b4-47b9-bf13-a57fa4e7248b.23.1"),sQuery(id+"F0.wireOp",EDGE,"2ae64cd4-93b4-47b9-bf13-a57fa4e7248b.24.0"),sQuery(id+"F0.wireOp",EDGE,"2ae64cd4-93b4-47b9-bf13-a57fa4e7248b.24.1"),sQuery(id+"F0.wireOp",EDGE,"2ae64cd4-93b4-47b9-bf13-a57fa4e7248b.25.0"),sQuery(id+"F0.wireOp",EDGE,"2ae64cd4-93b4-47b9-bf13-a57fa4e7248b.25.1"),sQuery(id+"F0.wireOp",EDGE,"2ae64cd4-93b4-47b9-bf13-a57fa4e7248b.26.0"),sQuery(id+"F0.wireOp",EDGE,"2ae64cd4-93b4-47b9-bf13-a57fa4e7248b.26.1"),sQuery(id+"F0.wireOp",EDGE,"2ae64cd4-93b4-47b9-bf13-a57fa4e7248b.27.0"),sQuery(id+"F0.wireOp",EDGE,"2ae64cd4-93b4-47b9-bf13-a57fa4e7248b.27.1"),sQuery(id+"F0.wireOp",EDGE,"2ae64cd4-93b4-47b9-bf13-a57fa4e7248b.28.0"),sQuery(id+"F0.wireOp",EDGE,"2ae64cd4-93b4-47b9-bf13-a57fa4e7248b.28.1"),sQuery(id+"F0.wireOp",EDGE,"2ae64cd4-93b4-47b9-bf13-a57fa4e7248b.29.0"),sQuery(id+"F0.wireOp",EDGE,"2ae64cd4-93b4-47b9-bf13-a57fa4e7248b.29.1"),sQuery(id+"F0.wireOp",EDGE,"2ae64cd4-93b4-47b9-bf13-a57fa4e7248b.30.0"),sQuery(id+"F0.wireOp",EDGE,"2ae64cd4-93b4-47b9-bf13-a57fa4e7248b.30.1"),sQuery(id+"F0.wireOp",EDGE,"2ae64cd4-93b4-47b9-bf13-a57fa4e7248b.31.0"),sQuery(id+"F0.wireOp",EDGE,"2ae64cd4-93b4-47b9-bf13-a57fa4e7248b.31.1"),sQuery(id+"F0.wireOp",EDGE,"2ae64cd4-93b4-47b9-bf13-a57fa4e7248b.32.0"),sQuery(id+"F0.wireOp",EDGE,"2ae64cd4-93b4-47b9-bf13-a57fa4e7248b.32.1"),sQuery(id+"F0.wireOp",EDGE,"2ae64cd4-93b4-47b9-bf13-a57fa4e7248b.33.0"),sQuery(id+"F0.wireOp",EDGE,"2ae64cd4-93b4-47b9-bf13-a57fa4e7248b.33.1"),sQuery(id+"F0.wireOp",EDGE,"2ae64cd4-93b4-47b9-bf13-a57fa4e7248b.34.0"),sQuery(id+"F0.wireOp",EDGE,"2ae64cd4-93b4-47b9-bf13-a57fa4e7248b.34.1"),sQuery(id+"F0.wireOp",EDGE,"2ae64cd4-93b4-47b9-bf13-a57fa4e7248b.35.0"),sQuery(id+"F0.wireOp",EDGE,"2ae64cd4-93b4-47b9-bf13-a57fa4e7248b.35.1"),sQuery(id+"F0.wireOp",EDGE,"2ae64cd4-93b4-47b9-bf13-a57fa4e7248b.36.0"),sQuery(id+"F0.wireOp",EDGE,"2ae64cd4-93b4-47b9-bf13-a57fa4e7248b.36.1"),sQuery(id+"F0.wireOp",EDGE,"2ae64cd4-93b4-47b9-bf13-a57fa4e7248b.37.0"),sQuery(id+"F0.wireOp",EDGE,"2ae64cd4-93b4-47b9-bf13-a57fa4e7248b.37.1"),sQuery(id+"F0.wireOp",EDGE,"2ae64cd4-93b4-47b9-bf13-a57fa4e7248b.38.0"),sQuery(id+"F0.wireOp",EDGE,"2ae64cd4-93b4-47b9-bf13-a57fa4e7248b.38.1"),sQuery(id+"F0.wireOp",EDGE,"2ae64cd4-93b4-47b9-bf13-a57fa4e7248b.39.0"),sQuery(id+"F0.wireOp",EDGE,"2ae64cd4-93b4-47b9-bf13-a57fa4e7248b.39.1"),sQuery(id+"F0.wireOp",EDGE,"2ae64cd4-93b4-47b9-bf13-a57fa4e7248b.40.0"),sQuery(id+"F0.wireOp",EDGE,"2ae64cd4-93b4-47b9-bf13-a57fa4e7248b.40.1"),sQuery(id+"F0.wireOp",EDGE,"2ae64cd4-93b4-47b9-bf13-a57fa4e7248b.41.0"),sQuery(id+"F0.wireOp",EDGE,"2ae64cd4-93b4-47b9-bf13-a57fa4e7248b.41.1"),sQuery(id+"F0.wireOp",EDGE,"2ae64cd4-93b4-47b9-bf13-a57fa4e7248b.42.0"),sQuery(id+"F0.wireOp",EDGE,"2ae64cd4-93b4-47b9-bf13-a57fa4e7248b.42.1"),sQuery(id+"F0.wireOp",EDGE,"2ae64cd4-93b4-47b9-bf13-a57fa4e7248b.43.0"),sQuery(id+"F0.wireOp",EDGE,"2ae64cd4-93b4-47b9-bf13-a57fa4e7248b.43.1"),sQuery(id+"F0.wireOp",EDGE,"2ae64cd4-93b4-47b9-bf13-a57fa4e7248b.44.0"),sQuery(id+"F0.wireOp",EDGE,"2ae64cd4-93b4-47b9-bf13-a57fa4e7248b.44.1"),sQuery(id+"F0.wireOp",EDGE,"2ae64cd4-93b4-47b9-bf13-a57fa4e7248b.45.0"),sQuery(id+"F0.wireOp",EDGE,"2ae64cd4-93b4-47b9-bf13-a57fa4e7248b.45.1"),sQuery(id+"F0.wireOp",EDGE,"2ae64cd4-93b4-47b9-bf13-a57fa4e7248b.46.0"),sQuery(id+"F0.wireOp",EDGE,"2ae64cd4-93b4-47b9-bf13-a57fa4e7248b.46.1"),sQuery(id+"F0.wireOp",EDGE,"2ae64cd4-93b4-47b9-bf13-a57fa4e7248b.47.0"),sQuery(id+"F0.wireOp",EDGE,"2ae64cd4-93b4-47b9-bf13-a57fa4e7248b.47.1"),sQuery(id+"F0.wireOp",EDGE,"2ae64cd4-93b4-47b9-bf13-a57fa4e7248b.48.0"),sQuery(id+"F0.wireOp",EDGE,"2ae64cd4-93b4-47b9-bf13-a57fa4e7248b.48.1"),sQuery(id+"F0.wireOp",EDGE,"2ae64cd4-93b4-47b9-bf13-a57fa4e7248b.49.0"),sQuery(id+"F0.wireOp",EDGE,"2ae64cd4-93b4-47b9-bf13-a57fa4e7248b.49.1")])],"isStart":false});
            var sketch = newSketch(context, id + "F2", { "sketchPlane" : qUnion([Q0])});
            skCircle(sketch, "E2", {"center": v(0, 0) * mm, "radius": 2.6 * mm});
            skCircle(sketch, "E3", {"center": v(0, 0) * mm, "radius": 1 * mm});
            skSolve(sketch);
        }
        {
            var Q0;
            Q0=makeQuery(id+"F2.imprint","IMPRINT",FACE,{"disambiguationData":[TD([[makeQuery(id+"F2.imprint","IMPRINT",EDGE,{"derivedFrom":sQuery(id+"F2.wireOp",EDGE,"E3")}),-1.0]])]});
            var Q1;
            {var subQ0=sQuery(id+"F2.wireOp",EDGE,"ef46eeef-f85e-4314-bc99-e56e5a110b71.1.0");Q1=makeQuery(id+"F2.imprint","IMPRINT",FACE,{"disambiguationData":[TD([[makeQuery(id+"F2.imprint","IMPRINT",EDGE,{"derivedFrom":subQ0}),-1.0]])]});}
            var Q2;
            {var subQ0=sQuery(id+"F2.wireOp",EDGE,"AXtbOmny-Rolw-DFvu-AzKX-92h4mGOaohQE");Q2=makeQuery(id+"F2.imprint","IMPRINT",FACE,{"disambiguationData":[TD([[makeQuery(id+"F2.imprint","IMPRINT",EDGE,{"derivedFrom":subQ0}),-1.0]])]});}
            var Q3;
            {var subQ0=sQuery(id+"F2.wireOp",EDGE,"ef46eeef-f85e-4314-bc99-e56e5a110b71.9.0");Q3=makeQuery(id+"F2.imprint","IMPRINT",FACE,{"disambiguationData":[TD([[makeQuery(id+"F2.imprint","IMPRINT",EDGE,{"derivedFrom":subQ0}),-1.0]])]});}
            var Q4;
            {var subQ0=sQuery(id+"F2.wireOp",EDGE,"ef46eeef-f85e-4314-bc99-e56e5a110b71.8.0");Q4=makeQuery(id+"F2.imprint","IMPRINT",FACE,{"disambiguationData":[TD([[makeQuery(id+"F2.imprint","IMPRINT",EDGE,{"derivedFrom":subQ0}),-1.0]])]});}
            var Q5;
            {var subQ0=sQuery(id+"F2.wireOp",EDGE,"ef46eeef-f85e-4314-bc99-e56e5a110b71.7.0");Q5=makeQuery(id+"F2.imprint","IMPRINT",FACE,{"disambiguationData":[TD([[makeQuery(id+"F2.imprint","IMPRINT",EDGE,{"derivedFrom":subQ0}),-1.0]])]});}
            var Q6;
            {var subQ0=sQuery(id+"F2.wireOp",EDGE,"ef46eeef-f85e-4314-bc99-e56e5a110b71.6.0");Q6=makeQuery(id+"F2.imprint","IMPRINT",FACE,{"disambiguationData":[TD([[makeQuery(id+"F2.imprint","IMPRINT",EDGE,{"derivedFrom":subQ0}),-1.0]])]});}
            var Q7;
            {var subQ0=sQuery(id+"F2.wireOp",EDGE,"ef46eeef-f85e-4314-bc99-e56e5a110b71.5.0");Q7=makeQuery(id+"F2.imprint","IMPRINT",FACE,{"disambiguationData":[TD([[makeQuery(id+"F2.imprint","IMPRINT",EDGE,{"derivedFrom":subQ0}),-1.0]])]});}
            var Q8;
            {var subQ0=sQuery(id+"F2.wireOp",EDGE,"ef46eeef-f85e-4314-bc99-e56e5a110b71.2.0");Q8=makeQuery(id+"F2.imprint","IMPRINT",FACE,{"disambiguationData":[TD([[makeQuery(id+"F2.imprint","IMPRINT",EDGE,{"derivedFrom":subQ0}),-1.0]])]});}
            var Q9;
            {var subQ0=sQuery(id+"F2.wireOp",EDGE,"ef46eeef-f85e-4314-bc99-e56e5a110b71.3.0");Q9=makeQuery(id+"F2.imprint","IMPRINT",FACE,{"disambiguationData":[TD([[makeQuery(id+"F2.imprint","IMPRINT",EDGE,{"derivedFrom":subQ0}),-1.0]])]});}
            var Q10;
            {var subQ0=sQuery(id+"F2.wireOp",EDGE,"ef46eeef-f85e-4314-bc99-e56e5a110b71.4.0");Q10=makeQuery(id+"F2.imprint","IMPRINT",FACE,{"disambiguationData":[TD([[makeQuery(id+"F2.imprint","IMPRINT",EDGE,{"derivedFrom":subQ0}),-1.0]])]});}
            var Q11;
            {var subQ0=sQuery(id+"F2.wireOp",EDGE,"6fafc8a2-5585-4b41-b53a-40911dd4761f.2.0");Q11=makeQuery(id+"F2.imprint","IMPRINT",FACE,{"disambiguationData":[TD([[makeQuery(id+"F2.imprint","IMPRINT",EDGE,{"derivedFrom":subQ0}),-1.0]])]});}
            var Q12;
            {var subQ0=sQuery(id+"F2.wireOp",EDGE,"6fafc8a2-5585-4b41-b53a-40911dd4761f.1.0");Q12=makeQuery(id+"F2.imprint","IMPRINT",FACE,{"disambiguationData":[TD([[makeQuery(id+"F2.imprint","IMPRINT",EDGE,{"derivedFrom":subQ0}),-1.0]])]});}
            var Q13;
            {var subQ0=sQuery(id+"F2.wireOp",EDGE,"6fafc8a2-5585-4b41-b53a-40911dd4761f.7.0");Q13=makeQuery(id+"F2.imprint","IMPRINT",FACE,{"disambiguationData":[TD([[makeQuery(id+"F2.imprint","IMPRINT",EDGE,{"derivedFrom":subQ0}),-1.0]])]});}
            var Q14;
            {var subQ0=sQuery(id+"F2.wireOp",EDGE,"6fafc8a2-5585-4b41-b53a-40911dd4761f.6.0");Q14=makeQuery(id+"F2.imprint","IMPRINT",FACE,{"disambiguationData":[TD([[makeQuery(id+"F2.imprint","IMPRINT",EDGE,{"derivedFrom":subQ0}),-1.0]])]});}
            var Q15;
            {var subQ0=sQuery(id+"F2.wireOp",EDGE,"6fafc8a2-5585-4b41-b53a-40911dd4761f.5.0");Q15=makeQuery(id+"F2.imprint","IMPRINT",FACE,{"disambiguationData":[TD([[makeQuery(id+"F2.imprint","IMPRINT",EDGE,{"derivedFrom":subQ0}),-1.0]])]});}
            var Q16;
            {var subQ0=sQuery(id+"F2.wireOp",EDGE,"6fafc8a2-5585-4b41-b53a-40911dd4761f.4.0");Q16=makeQuery(id+"F2.imprint","IMPRINT",FACE,{"disambiguationData":[TD([[makeQuery(id+"F2.imprint","IMPRINT",EDGE,{"derivedFrom":subQ0}),-1.0]])]});}
            var Q17;
            {var subQ0=sQuery(id+"F2.wireOp",EDGE,"6fafc8a2-5585-4b41-b53a-40911dd4761f.3.0");Q17=makeQuery(id+"F2.imprint","IMPRINT",FACE,{"disambiguationData":[TD([[makeQuery(id+"F2.imprint","IMPRINT",EDGE,{"derivedFrom":subQ0}),-1.0]])]});}
            extrude(context, id + "F3", {"entities" : qUnion([Q0, Q1, Q2, Q3, Q4, Q5, Q6, Q7, Q8, Q9, Q10, Q11, Q12, Q13, Q14, Q15, Q16, Q17]), "operationType" : NewBodyOperationType.ADD, "depth" : 3.8 * mm, "offsetDistance" : 25 * mm});
        }
        {
            var Q0;
            Q0=qCreatedBy(makeId("Top.planeOp"),FACE);
            var sketch = newSketch(context, id + "F4", { "sketchPlane" : qUnion([Q0])});
            skCircle(sketch, "E4", {"center": v(27.34, 0) * mm, "radius": 10 * mm});
            skCircle(sketch, "E5", {"center": v(59.93, 0) * mm, "radius": 12.5 * mm});
            skCircle(sketch, "E6", {"center": v(-21.98, 0) * mm, "radius": 6.5 * mm});
            skCircle(sketch, "E7", {"center": v(-42.37, 0) * mm, "radius": 5 * mm});
            skCircle(sketch, "E8", {"center": v(-58.44, 0) * mm, "radius": 2.5 * mm});
            skCircle(sketch, "E9", {"center": v(59.93, 0) * mm, "radius": 1 * mm});
            skCircle(sketch, "E10", {"center": v(27.34, 0) * mm, "radius": 1 * mm});
            skCircle(sketch, "E11", {"center": v(-21.98, 0) * mm, "radius": 1 * mm});
            skCircle(sketch, "E12", {"center": v(-42.37, 0) * mm, "radius": 1 * mm});
            skCircle(sketch, "E13", {"center": v(-58.44, 0) * mm, "radius": 1 * mm});
            skSolve(sketch);
        }
        {
            var Q0;
            Q0=makeQuery(id+"F4.imprint","IMPRINT",FACE,{"disambiguationData":[TD([[makeQuery(id+"F4.imprint","IMPRINT",EDGE,{"derivedFrom":sQuery(id+"F4.wireOp",EDGE,"E4")}),1.0]])]});
            var Q1;
            Q1=makeQuery(id+"F4.imprint","IMPRINT",FACE,{"disambiguationData":[TD([[makeQuery(id+"F4.imprint","IMPRINT",EDGE,{"derivedFrom":sQuery(id+"F4.wireOp",EDGE,"E5")}),1.0]])]});
            var Q2;
            Q2=makeQuery(id+"F4.imprint","IMPRINT",FACE,{"disambiguationData":[TD([[makeQuery(id+"F4.imprint","IMPRINT",EDGE,{"derivedFrom":sQuery(id+"F4.wireOp",EDGE,"E6")}),1.0]])]});
            var Q3;
            Q3=makeQuery(id+"F4.imprint","IMPRINT",FACE,{"disambiguationData":[TD([[makeQuery(id+"F4.imprint","IMPRINT",EDGE,{"derivedFrom":sQuery(id+"F4.wireOp",EDGE,"E7")}),1.0]])]});
            var Q4;
            Q4=makeQuery(id+"F4.imprint","IMPRINT",FACE,{"disambiguationData":[TD([[makeQuery(id+"F4.imprint","IMPRINT",EDGE,{"derivedFrom":sQuery(id+"F4.wireOp",EDGE,"E8")}),1.0]])]});
            extrude(context, id + "F5", {"entities" : qUnion([Q0, Q1, Q2, Q3, Q4]), "depth" : 1.5 * mm, "offsetDistance" : 25 * mm});
        }
        {
            var Q0;
            Q0=makeQuery(id+"F5.opExtrude","CAP_FACE",FACE,{"disambiguationData":[OSD([sQuery(id+"F4.wireOp",EDGE,"E4"),sQuery(id+"F4.wireOp",EDGE,"E10")])],"isStart":false});
            var sketch = newSketch(context, id + "F6", { "sketchPlane" : qUnion([Q0])});
            skCircle(sketch, "E14", {"center": v(27.34, 0) * mm, "radius": 2.6 * mm});
            skSolve(sketch);
        }
        {
            var Q0;
            Q0=makeQuery(id+"F6.imprint","IMPRINT",FACE,{"disambiguationData":[TD([[makeQuery(id+"F6.imprint","IMPRINT",EDGE,{"derivedFrom":sQuery(id+"F6.wireOp",EDGE,"E14")}),1.0]])]});
            extrude(context, id + "F7", {"entities" : qUnion([Q0]), "operationType" : NewBodyOperationType.ADD, "depth" : 3.8 * mm, "offsetDistance" : 25 * mm});
        }
        {
            var Q0;
            Q0=makeQuery(id+"F5.opExtrude","CAP_FACE",FACE,{"disambiguationData":[OSD([sQuery(id+"F4.wireOp",EDGE,"E5"),sQuery(id+"F4.wireOp",EDGE,"E9")])],"isStart":false});
            var sketch = newSketch(context, id + "F8", { "sketchPlane" : qUnion([Q0])});
            skCircle(sketch, "E15", {"center": v(59.93, 0) * mm, "radius": 2.6 * mm});
            skSolve(sketch);
        }
        {
            var Q0;
            Q0=makeQuery(id+"F8.imprint","IMPRINT",FACE,{"disambiguationData":[TD([[makeQuery(id+"F8.imprint","IMPRINT",EDGE,{"derivedFrom":sQuery(id+"F8.wireOp",EDGE,"E15")}),1.0]])]});
            extrude(context, id + "F9", {"entities" : qUnion([Q0]), "operationType" : NewBodyOperationType.ADD, "depth" : 3.8 * mm, "offsetDistance" : 25 * mm});
        }
        {
            var Q0;
            Q0=makeQuery(id+"F5.opExtrude","CAP_FACE",FACE,{"disambiguationData":[OSD([sQuery(id+"F4.wireOp",EDGE,"E6"),sQuery(id+"F4.wireOp",EDGE,"E11")])],"isStart":false});
            var sketch = newSketch(context, id + "F10", { "sketchPlane" : qUnion([Q0])});
            skCircle(sketch, "E16", {"center": v(-21.98, 0) * mm, "radius": 2.1 * mm});
            skSolve(sketch);
        }
        {
            var Q0;
            Q0=makeQuery(id+"F10.imprint","IMPRINT",FACE,{"disambiguationData":[TD([[makeQuery(id+"F10.imprint","IMPRINT",EDGE,{"derivedFrom":sQuery(id+"F10.wireOp",EDGE,"E16")}),1.0]])]});
            extrude(context, id + "F11", {"entities" : qUnion([Q0]), "operationType" : NewBodyOperationType.ADD, "depth" : 3.8 * mm, "offsetDistance" : 25 * mm});
        }
        {
            var Q0;
            Q0=makeQuery(id+"F5.opExtrude","CAP_FACE",FACE,{"disambiguationData":[OSD([sQuery(id+"F4.wireOp",EDGE,"E7"),sQuery(id+"F4.wireOp",EDGE,"E12")])],"isStart":false});
            var sketch = newSketch(context, id + "F12", { "sketchPlane" : qUnion([Q0])});
            skCircle(sketch, "E17", {"center": v(-42.37, 0) * mm, "radius": 2.1 * mm});
            skSolve(sketch);
        }
        {
            var Q0;
            Q0=makeQuery(id+"F12.imprint","IMPRINT",FACE,{"disambiguationData":[TD([[makeQuery(id+"F12.imprint","IMPRINT",EDGE,{"derivedFrom":sQuery(id+"F12.wireOp",EDGE,"E17")}),1.0]])]});
            extrude(context, id + "F13", {"entities" : qUnion([Q0]), "operationType" : NewBodyOperationType.ADD, "depth" : 3.8 * mm, "offsetDistance" : 25 * mm});
        }
        {
            var Q0;
            Q0=makeQuery(id+"F5.opExtrude","CAP_FACE",FACE,{"disambiguationData":[OSD([sQuery(id+"F4.wireOp",EDGE,"E8"),sQuery(id+"F4.wireOp",EDGE,"E13")])],"isStart":false});
            extrude(context, id + "F14", {"entities" : qUnion([Q0]), "operationType" : NewBodyOperationType.ADD, "depth" : 2 * mm, "offsetDistance" : 25 * mm});
        }
        {
            var Q0;
            Q0=qCreatedBy(makeId("Top.planeOp"),FACE);
            var sketch = newSketch(context, id + "F15", { "sketchPlane" : qUnion([Q0])});
            skCircle(sketch, "E18", {"center": v(90.84, 0) * mm, "radius": 14 * mm});
            skCircle(sketch, "E19", {"center": v(90.84, 0) * mm, "radius": 1 * mm});
            skSolve(sketch);
        }
        {
            var Q0;
            Q0 = qSketchRegion(id + "F15", true);
            var Q1;
            Q1=makeQuery(id+"F15.imprint","IMPRINT",FACE,{"disambiguationData":[TD([[makeQuery(id+"F15.imprint","IMPRINT",EDGE,{"derivedFrom":sQuery(id+"F15.wireOp",EDGE,"E18")}),1.0]])]});
            extrude(context, id + "F16", {"entities" : qUnion([Q0, Q1]), "depth" : 1.5 * mm, "offsetDistance" : 25 * mm});
        }
    });
